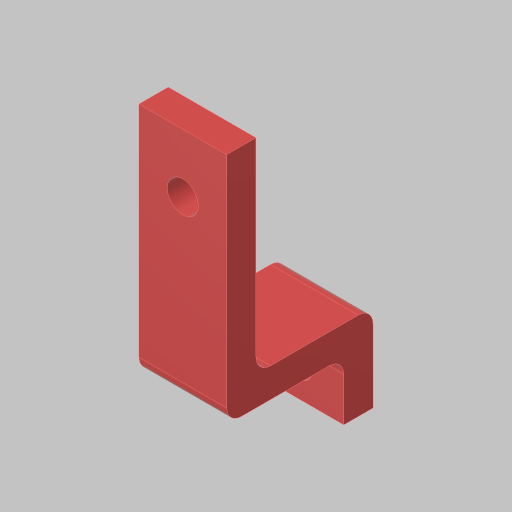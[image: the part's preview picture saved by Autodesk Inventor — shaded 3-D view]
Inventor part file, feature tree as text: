
AUTODESK INVENTOR PART (.ipt)
format: ipt  version: 2023.5 (Build 275446000, 446)  size: 120,320 bytes
history: native  units: in
note: dims shown in document units (in); Inventor stores cm internally (conversion verified against a paired STEP export)
features: sketch x3, hole x2, extrude x1, fillet x1
ambient origin geometry x8: Origin, YZ Plane, XZ Plane, XY Plane, X Axis, Y Axis, Z Axis, Center Point
bodies: Solid1 (feature_tree)
feature tree (7):
  extrude  "Extrusion1"  Depth=1.0in
  hole  "Hole1"  [1 undecoded]
  hole  "Hole2"  [1 undecoded]
  fillet  "Fillet1"  Radius=0.5in
  sketch  "Sketch1"  dims[d0=2.0in d1=1.0in]
  sketch  "Sketch2"  dims[d2=0.5in d3=0.25in]
  sketch  "Sketch3"  dims[d4=0.75in d5=0.0in d6=0.266in d7=0.75in d8=0.507in d9=0.25in d10=0.5635in d11=1.0in d12=0.8108in d13=0.201in d14=0.75in d15=0.385in d16=0.25in d17=0.5635in d18=1.0in d19=0.8108in d20=0.125in d21=0.5in]
note: 2 required parameter values undecoded (feature->parameter linkage not recoverable at this tier; creation-order binding heuristic only, values carry confidence <= 0.55)
